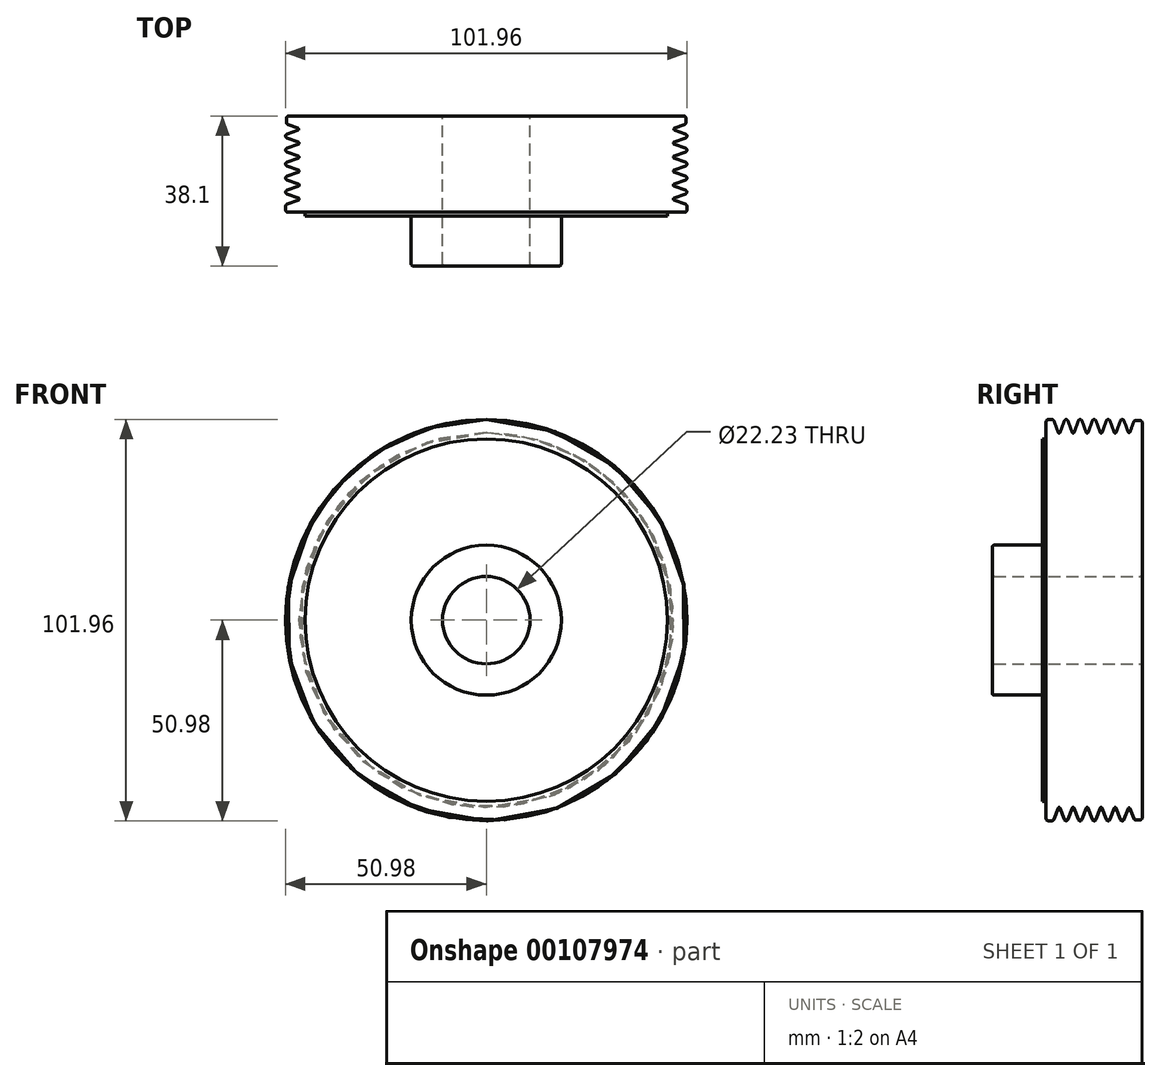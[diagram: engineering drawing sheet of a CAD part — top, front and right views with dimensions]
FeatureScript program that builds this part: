
annotation { "Feature Type Name" : "Feature", "Feature Type Description" : "" }
export const myFeature = defineFeature(function(context is Context, id is Id, definition is map)
    precondition{}
    {
        {
            var Q0;
            Q0=qCreatedBy(makeId("Front.planeOp"),FACE);
            var sketch = newSketch(context, id + "F0", { "sketchPlane" : qUnion([Q0])});
            skCircle(sketch, "E0", {"center": v(0, 0) * mm, "radius": 50.8 * mm});
            skCircle(sketch, "E1", {"center": v(0, 0) * mm, "radius": 11.11 * mm});
            skCircle(sketch, "E2", {"center": v(0, 0) * mm, "radius": 19.05 * mm});
            skCircle(sketch, "E3", {"center": v(0, 0) * mm, "radius": 46.02 * mm});
            skSolve(sketch);
        }
        {
            var Q0;
            Q0=qCreatedBy(makeId("Right.planeOp"),FACE);
            var sketch = newSketch(context, id + "F1", { "sketchPlane" : qUnion([Q0])});
            skArc(sketch, "E4", {"start": v(-3.57, 47.82) * mm, "mid": v(-3.56, 47.8) * mm, "end": v(-3.55, 47.78) * mm});
            skLineSegment(sketch, "E5", {"start": v(-3.57, 47.82) * mm, "end": v(-4.6, 50.65) * mm});
            skLineSegment(sketch, "E6", {"start": v(-5.56, 50.65) * mm, "end": v(-6.62, 47.7) * mm});
            skArc(sketch, "E7", {"start": v(-4.6, 50.65) * mm, "mid": v(-5.08, 50.98) * mm, "end": v(-5.56, 50.65) * mm});
            skLineSegment(sketch, "E8", {"start": v(-7.1, 47.7) * mm, "end": v(-8.17, 50.63) * mm});
            skLineSegment(sketch, "E9", {"start": v(-9.12, 50.63) * mm, "end": v(-10.18, 47.71) * mm});
            skArc(sketch, "E10", {"start": v(-7.1, 47.7) * mm, "mid": v(-6.86, 47.54) * mm, "end": v(-6.62, 47.7) * mm});
            skArc(sketch, "E11", {"start": v(-10.66, 47.71) * mm, "mid": v(-10.42, 47.55) * mm, "end": v(-10.18, 47.71) * mm});
            skArc(sketch, "E12", {"start": v(-8.17, 50.63) * mm, "mid": v(-8.64, 50.96) * mm, "end": v(-9.12, 50.63) * mm});
            skLineSegment(sketch, "E13", {"start": v(-10.66, 47.71) * mm, "end": v(-11.72, 50.63) * mm});
            skLineSegment(sketch, "E14", {"start": v(-12.67, 50.63) * mm, "end": v(-13.74, 47.7) * mm});
            skArc(sketch, "E15", {"start": v(-11.72, 50.63) * mm, "mid": v(-12.2, 50.96) * mm, "end": v(-12.67, 50.63) * mm});
            skLineSegment(sketch, "E16", {"start": v(-10.66, 47.7) * mm, "end": v(-11.72, 50.63) * mm});
            skArc(sketch, "E17", {"start": v(-10.66, 47.7) * mm, "mid": v(-10.56, 47.59) * mm, "end": v(-10.42, 47.54) * mm});
            skArc(sketch, "E18", {"start": v(-14.21, 47.7) * mm, "mid": v(-13.98, 47.54) * mm, "end": v(-13.74, 47.7) * mm});
            skLineSegment(sketch, "E19", {"start": v(-14.21, 47.7) * mm, "end": v(-15.28, 50.62) * mm});
            skLineSegment(sketch, "E20", {"start": v(-16.23, 50.62) * mm, "end": v(-17.3, 47.69) * mm});
            skArc(sketch, "E21", {"start": v(-15.28, 50.62) * mm, "mid": v(-15.75, 50.96) * mm, "end": v(-16.23, 50.62) * mm});
            skLineSegment(sketch, "E22", {"start": v(-17.78, 47.69) * mm, "end": v(-18.84, 50.6) * mm});
            skLineSegment(sketch, "E23", {"start": v(-19.8, 50.6) * mm, "end": v(-20.86, 47.7) * mm});
            skArc(sketch, "E24", {"start": v(-17.78, 47.69) * mm, "mid": v(-17.54, 47.52) * mm, "end": v(-17.3, 47.69) * mm});
            skArc(sketch, "E25", {"start": v(-21.33, 47.7) * mm, "mid": v(-21.1, 47.53) * mm, "end": v(-20.86, 47.7) * mm});
            skArc(sketch, "E26", {"start": v(-18.84, 50.6) * mm, "mid": v(-19.32, 50.94) * mm, "end": v(-19.8, 50.6) * mm});
            skLineSegment(sketch, "E27", {"start": v(-21.33, 47.7) * mm, "end": v(-22.4, 50.6) * mm});
            skArc(sketch, "E28", {"start": v(-22.4, 50.6) * mm, "mid": v(-22.58, 50.85) * mm, "end": v(-22.87, 50.94) * mm});
            skLineSegment(sketch, "E29", {"start": v(-21.33, 47.69) * mm, "end": v(-22.4, 50.6) * mm});
            skArc(sketch, "E30", {"start": v(-21.33, 47.69) * mm, "mid": v(-21.24, 47.57) * mm, "end": v(-21.1, 47.52) * mm});
            skPoint(sketch, "E31.orphan", {"position": v(-3.55, 48.72) * mm});
            skArc(sketch, "E32", {"start": v(-3.55, 47.78) * mm, "mid": v(-3.31, 47.65) * mm, "end": v(-3.1, 47.82) * mm});
            skLineSegment(sketch, "E33", {"start": v(-22.87, 50.94) * mm, "end": v(-24.4, 50.94) * mm});
            skPoint(sketch, "E34.orphan", {"position": v(0, 46.89) * mm});
            skLineSegment(sketch, "E35", {"start": v(-24.4, 44.3) * mm, "end": v(0, 44.3) * mm});
            skLineSegment(sketch, "E36", {"start": v(-24.4, 50.94) * mm, "end": v(-24.4, 44.3) * mm});
            skLineSegment(sketch, "E37", {"start": v(0, 46.89) * mm, "end": v(0, 44.3) * mm});
            skLineSegment(sketch, "E38", {"start": v(-3.1, 47.82) * mm, "end": v(-2.04, 50.71) * mm});
            skLineSegment(sketch, "E39", {"start": v(-2.04, 50.71) * mm, "end": v(0, 50.71) * mm});
            skLineSegment(sketch, "E40", {"start": v(0, 50.71) * mm, "end": v(0, 46.89) * mm});
            skSolve(sketch);
        }
        {
            var Q0;
            Q0 = qSketchRegion(id + "F1", true);
            var Q1;
            Q1=sQuery(id+"F0.wireOp",EDGE,"E0");
            sweep(context, id + "F2", {"profiles" : qUnion([Q0]), "path" : qUnion([Q1])});
        }
        {
            var Q0;
            Q0=makeQuery(id+"F0.imprint","IMPRINT",FACE,{"disambiguationData":[TD([[makeQuery(id+"F0.imprint","IMPRINT",EDGE,{"derivedFrom":sQuery(id+"F0.wireOp",EDGE,"E1")}),-1.0]])]});
            extrude(context, id + "F3", {"entities" : qUnion([Q0]), "operationType" : NewBodyOperationType.ADD, "depth" : 38.1 * mm});
        }
        {
            var Q0;
            Q0=makeQuery(id+"F0.imprint","IMPRINT",FACE,{"disambiguationData":[TD([[makeQuery(id+"F0.imprint","IMPRINT",EDGE,{"derivedFrom":sQuery(id+"F0.wireOp",EDGE,"E2")}),-1.0]])]});
            extrude(context, id + "F4", {"entities" : qUnion([Q0]), "operationType" : NewBodyOperationType.ADD, "depth" : 25.4 * mm});
        }
        {
            var Q0;
            Q0=makeQuery(id+"F2.opSweep","SWEPT_FACE",FACE,{"disambiguationData":[OSD([sQuery(id+"F0.wireOp",EDGE,"E0"),sQuery(id+"F1.wireOp",EDGE,"gOgDP8lk-GxNq-blme-97cy-HSxHVtbo0r4c")])]});
            var Q1;
            Q1=makeQuery(id+"F2.opSweep","SWEPT_EDGE",EDGE,{"disambiguationData":[OSD([sQuery(id+"F0.wireOp",EDGE,"E0"),sQuery(id+"F1.wireOp",EDGE,"gOgDP8lk-GxNq-blme-97cy-HSxHVtbo0r4c"),sQuery(id+"F1.wireOp",EDGE,"koeX9DQb-psej-mURh-Skbm-ir8ML7w1tz4M")])]});
            var Q2;
            Q2=makeQuery(id+"F2.opSweep","SWEPT_FACE",FACE,{"disambiguationData":[OSD([sQuery(id+"F0.wireOp",EDGE,"E0"),sQuery(id+"F1.wireOp",EDGE,"E33")])]});
            var Q3;
            Q3=makeQuery(id+"F2.opSweep","SWEPT_EDGE",EDGE,{"disambiguationData":[OSD([sQuery(id+"F0.wireOp",EDGE,"E0"),sQuery(id+"F1.wireOp",EDGE,"7Z3Ze1Nv-J0Y8-mVAp-EnZf-AwHmyvBVf9W7.right"),sQuery(id+"F1.wireOp",EDGE,"E33")])]});
            var Q4;
            Q4=makeQuery(id+"F3.opExtrude","CAP_EDGE",EDGE,{"disambiguationData":[OSD([sQuery(id+"F0.wireOp",EDGE,"E0")])],"isStart":true});
            var Q5;
            Q5=makeQuery(id+"F2.opSweep","SWEPT_EDGE",EDGE,{"disambiguationData":[OSD([sQuery(id+"F0.wireOp",EDGE,"E0"),sQuery(id+"F1.wireOp",EDGE,"7Z3Ze1Nv-J0Y8-mVAp-EnZf-AwHmyvBVf9W7.bottom"),sQuery(id+"F1.wireOp",EDGE,"koeX9DQb-psej-mURh-Skbm-ir8ML7w1tz4M")])]});
            var Q6;
            Q6=makeQuery(id+"F2.opSweep","SWEPT_EDGE",EDGE,{"disambiguationData":[OSD([sQuery(id+"F0.wireOp",EDGE,"E0"),sQuery(id+"F1.wireOp",EDGE,"7Z3Ze1Nv-J0Y8-mVAp-EnZf-AwHmyvBVf9W7.bottom"),sQuery(id+"F1.wireOp",EDGE,"7Z3Ze1Nv-J0Y8-mVAp-EnZf-AwHmyvBVf9W7.right")])]});
            var Q7;
            Q7=makeQuery(id+"F3.opExtrude","CAP_EDGE",EDGE,{"disambiguationData":[OSD([sQuery(id+"F0.wireOp",EDGE,"E2")])],"isStart":false});
            var Q8;
            Q8=makeQuery(id+"F3.opExtrude","CAP_EDGE",EDGE,{"disambiguationData":[OSD([sQuery(id+"F0.wireOp",EDGE,"E1")])],"isStart":false});
            var Q9;
            Q9=makeQuery(id+"F3.opExtrude","CAP_EDGE",EDGE,{"disambiguationData":[OSD([sQuery(id+"F0.wireOp",EDGE,"E1")])],"isStart":true});
            var Q10;
            Q10=makeQuery(id+"F4.opExtrude","CAP_EDGE",EDGE,{"disambiguationData":[OSD([sQuery(id+"F0.wireOp",EDGE,"E2")])],"isStart":false});
            fillet(context, id + "F5", {"entities" : qUnion([Q0, Q1, Q2, Q3, Q4, Q5, Q6, Q7, Q8, Q9, Q10]), "radius" : 0.5 * mm, "tangentPropagation" : true, "allowEdgeOverflow" : false});
        }
    });
